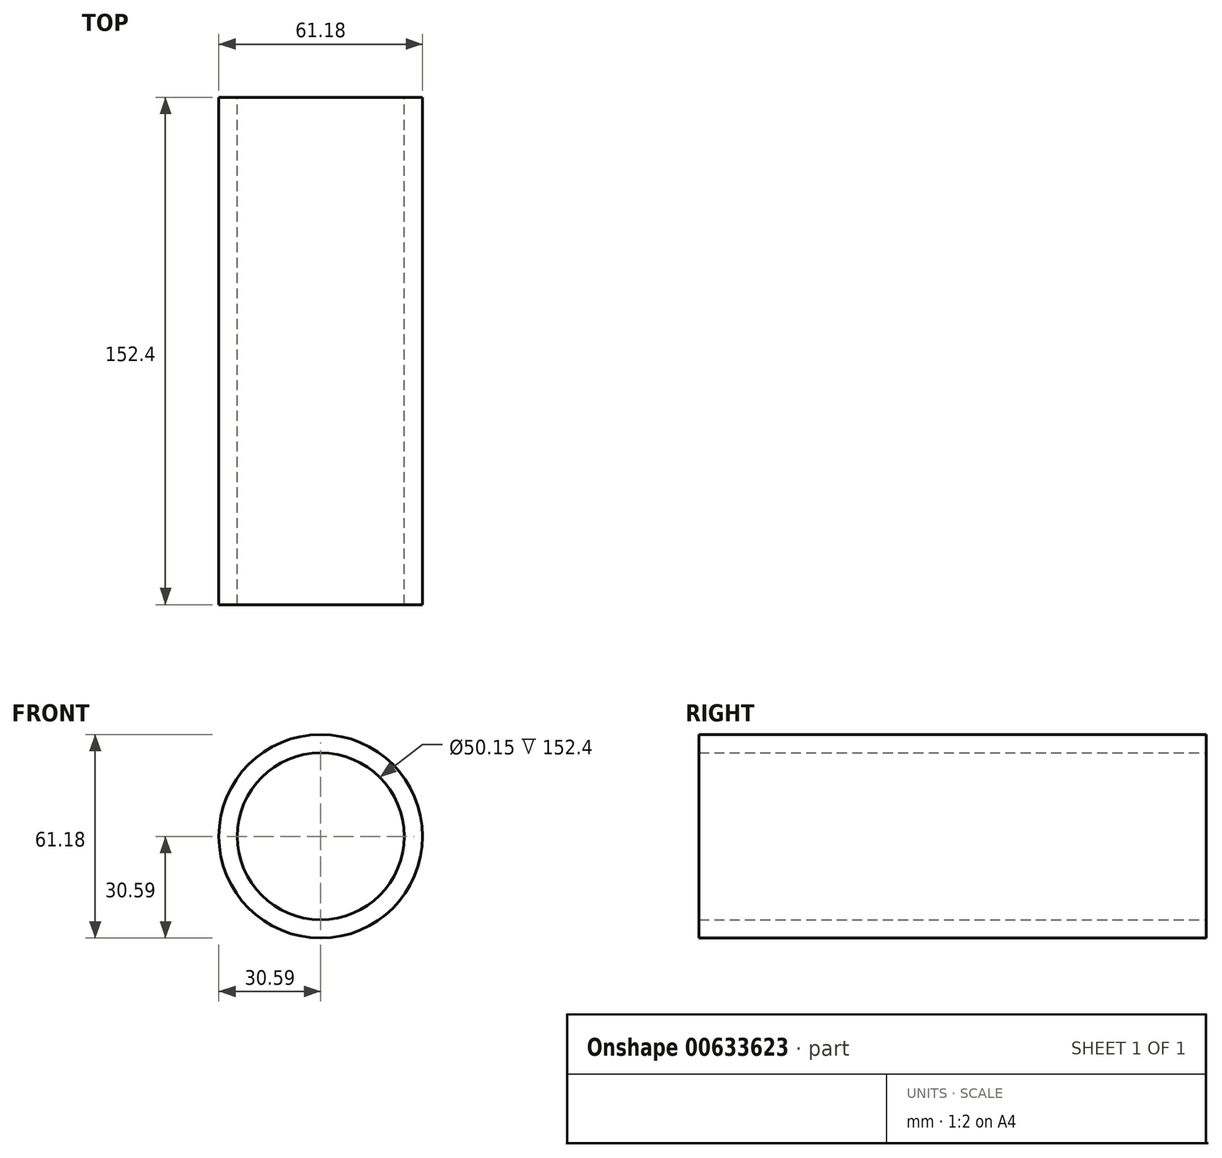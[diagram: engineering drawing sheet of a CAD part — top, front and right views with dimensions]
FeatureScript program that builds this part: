
annotation { "Feature Type Name" : "Feature", "Feature Type Description" : "" }
export const myFeature = defineFeature(function(context is Context, id is Id, definition is map)
    precondition{}
    {
        {
            var Q0;
            Q0=qCreatedBy(makeId("Front.planeOp"),FACE);
            var sketch = newSketch(context, id + "F0", { "sketchPlane" : qUnion([Q0])});
            skCircle(sketch, "E0", {"center": v(0, 0) * mm, "radius": 25.07 * mm});
            skCircle(sketch, "E1", {"center": v(0, 0) * mm, "radius": 30.59 * mm});
            skSolve(sketch);
        }
        {
            var Q0;
            Q0 = qSketchRegion(id + "F0", true);
            extrude(context, id + "F1", {"entities" : qUnion([Q0]), "depth" : 152.4 * mm, "offsetDistance" : 25.4 * mm});
        }
    });
